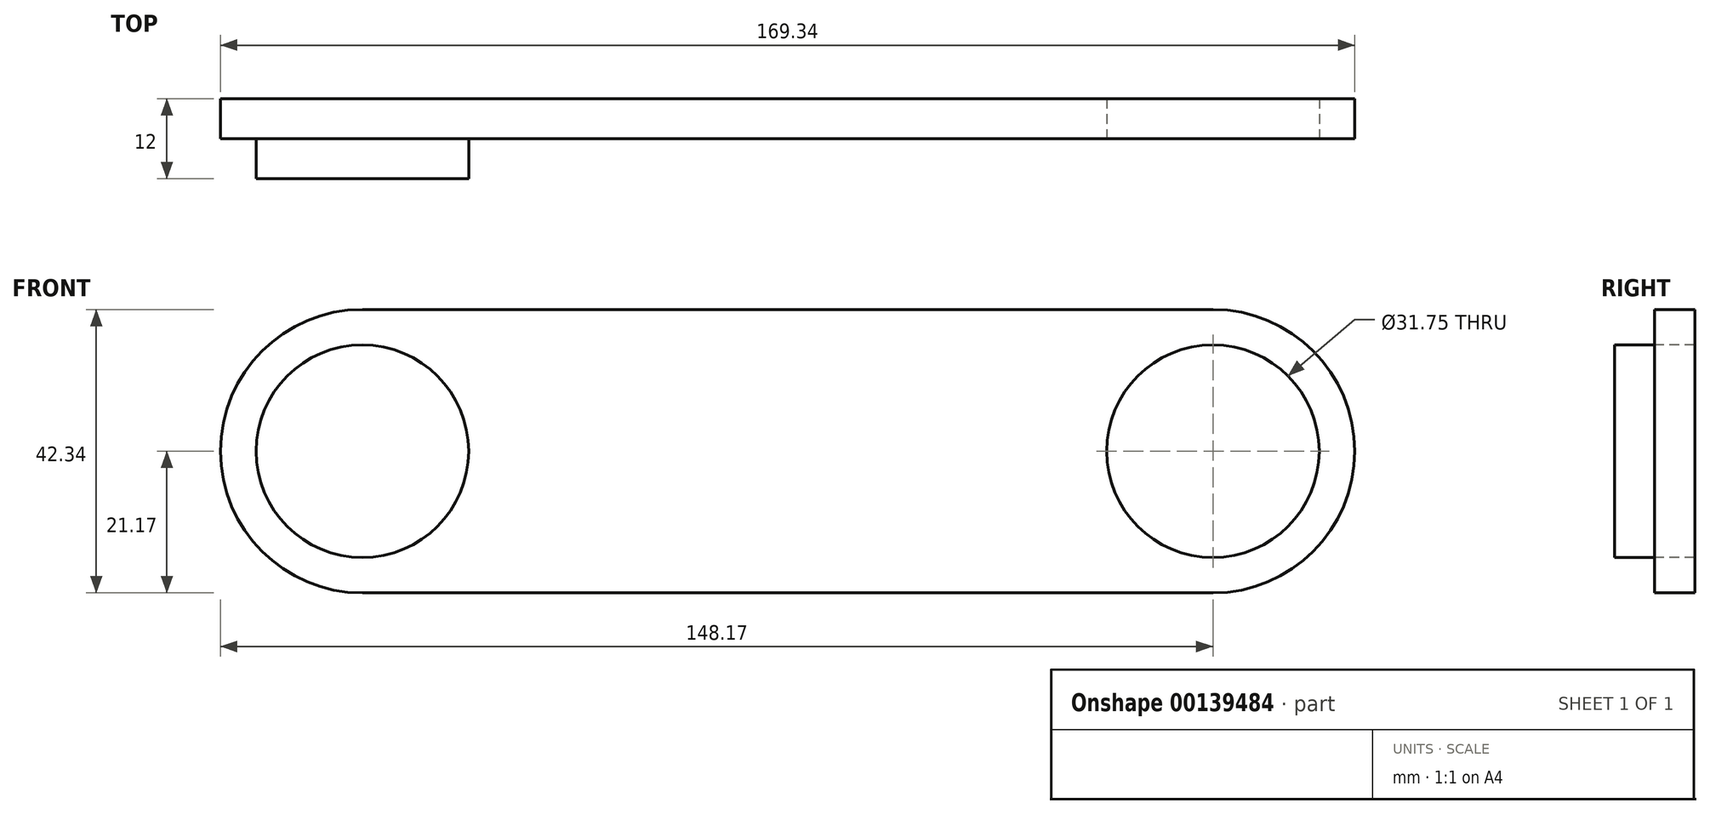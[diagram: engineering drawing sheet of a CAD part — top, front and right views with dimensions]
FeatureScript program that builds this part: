
annotation { "Feature Type Name" : "Feature", "Feature Type Description" : "" }
export const myFeature = defineFeature(function(context is Context, id is Id, definition is map)
    precondition{}
    {
        {
            assignVariable(context, id + "F0", {"name" : "depth", "anyValue" : 6});
        }
        {
            var Q0;
            Q0=qCreatedBy(makeId("Front.planeOp"),FACE);
            var sketch = newSketch(context, id + "F1", { "sketchPlane" : qUnion([Q0])});
            skLineSegment(sketch, "E0.bottom", {"start": v(-63.5, 21.17) * mm, "end": v(63.5, 21.17) * mm});
            skLineSegment(sketch, "E0.top", {"start": v(-63.5, -21.17) * mm, "end": v(63.5, -21.17) * mm});
            skPoint(sketch, "E0.middle", {"position": v(0, 0) * mm});
            skArc(sketch, "E1", {"start": v(-63.5, 21.17) * mm, "mid": v(-84.67, 0) * mm, "end": v(-63.5, -21.17) * mm});
            skArc(sketch, "E2", {"start": v(63.5, 21.17) * mm, "mid": v(84.67, 0) * mm, "end": v(63.5, -21.17) * mm});
            skLineSegment(sketch, "E3", {"start": v(-63.5, 21.17) * mm, "end": v(-63.5, -21.17) * mm, "construction": true});
            skLineSegment(sketch, "E4", {"start": v(63.5, 21.17) * mm, "end": v(63.5, -21.17) * mm, "construction": true});
            skSolve(sketch);
        }
        {
            var Q0;
            Q0 = qSketchRegion(id + "F1", true);
            extrude(context, id + "F2", {"entities" : qUnion([Q0]), "depth" : (getVariable(context, 'depth')) * mm});
        }
        {
            var Q0;
            Q0=makeQuery(id+"F2.opExtrude","CAP_FACE",FACE,{"disambiguationData":[OSD([sQuery(id+"F1.wireOp",EDGE,"E0.bottom"),sQuery(id+"F1.wireOp",EDGE,"E0.top"),sQuery(id+"F1.wireOp",EDGE,"E1"),sQuery(id+"F1.wireOp",EDGE,"E2")])],"isStart":false});
            var sketch = newSketch(context, id + "F3", { "sketchPlane" : qUnion([Q0])});
            skCircle(sketch, "E5", {"center": v(-63.5, 0) * mm, "radius": 15.88 * mm});
            skSolve(sketch);
        }
        {
            var Q0;
            Q0 = qSketchRegion(id + "F3", true);
            extrude(context, id + "F4", {"entities" : qUnion([Q0]), "operationType" : NewBodyOperationType.ADD, "depth" : (getVariable(context, 'depth')) * mm});
        }
        {
            var Q0;
            Q0=makeQuery(id+"F2.opExtrude","CAP_FACE",FACE,{"disambiguationData":[OSD([sQuery(id+"F1.wireOp",EDGE,"E0.bottom"),sQuery(id+"F1.wireOp",EDGE,"E0.top"),sQuery(id+"F1.wireOp",EDGE,"E1"),sQuery(id+"F1.wireOp",EDGE,"E2")])],"isStart":false});
            var sketch = newSketch(context, id + "F5", { "sketchPlane" : qUnion([Q0])});
            skCircle(sketch, "E6", {"center": v(63.5, 0) * mm, "radius": 15.88 * mm});
            skSolve(sketch);
        }
        {
            var Q0;
            Q0 = qSketchRegion(id + "F5", true);
            extrude(context, id + "F6", {"entities" : qUnion([Q0]), "operationType" : NewBodyOperationType.REMOVE, "oppositeDirection" : true, "depth" : (getVariable(context, 'depth')) * mm});
        }
    });
